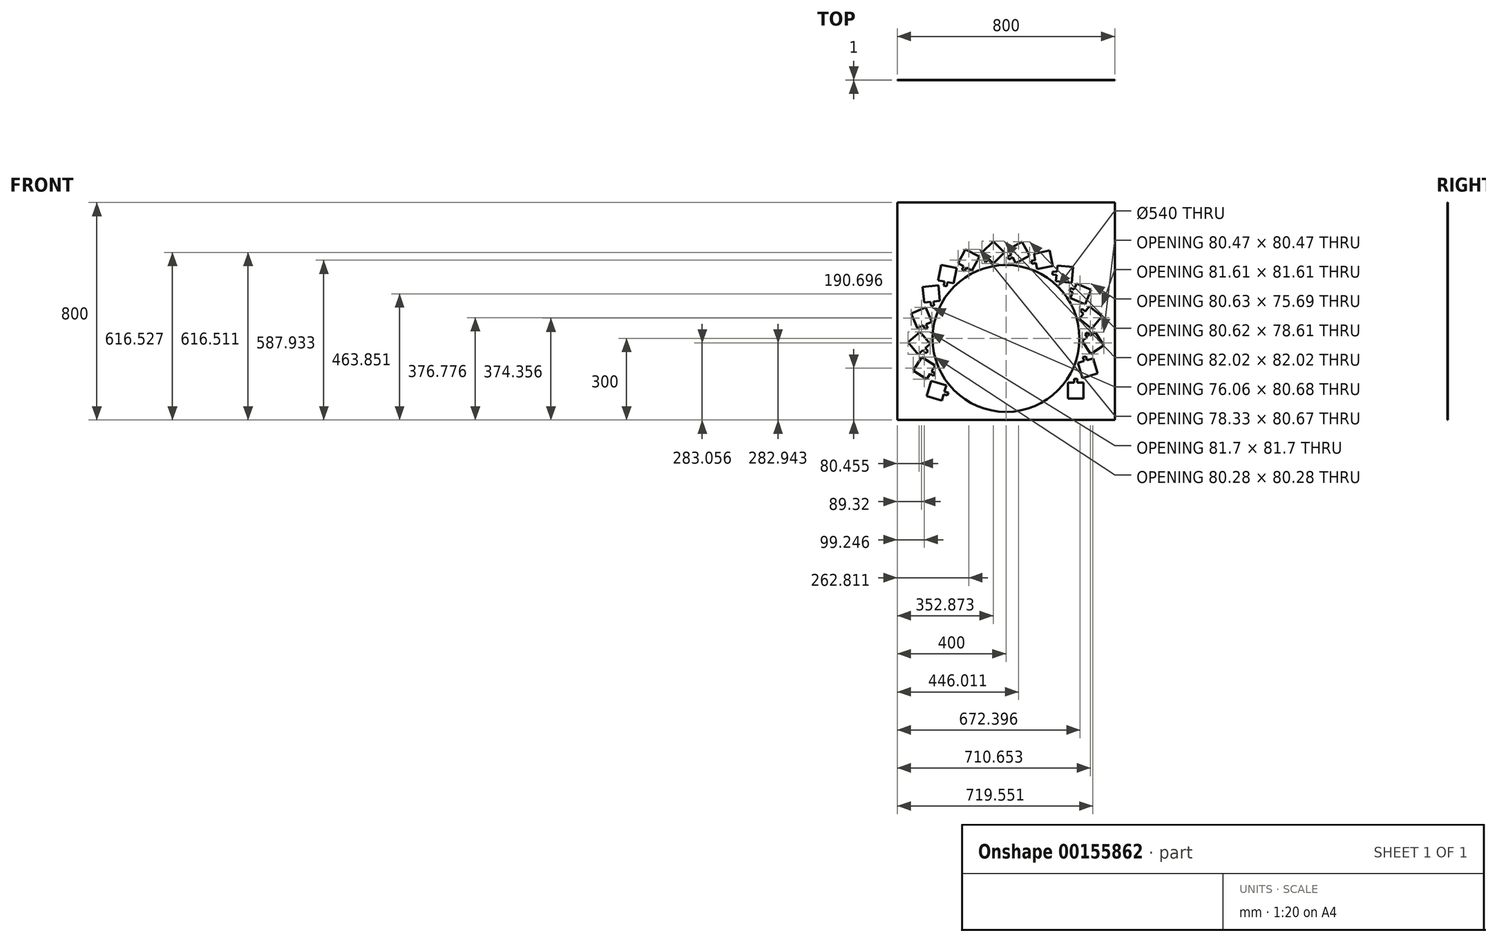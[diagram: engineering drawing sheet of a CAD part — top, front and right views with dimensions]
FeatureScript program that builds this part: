
annotation { "Feature Type Name" : "Feature", "Feature Type Description" : "" }
export const myFeature = defineFeature(function(context is Context, id is Id, definition is map)
    precondition{}
    {
        {
            var Q0;
            Q0=qCreatedBy(makeId("Front.planeOp"),FACE);
            var sketch = newSketch(context, id + "F0", { "sketchPlane" : qUnion([Q0])});
            skLineSegment(sketch, "E0.bottom", {"start": v(-400, 400) * mm, "end": v(400, 400) * mm});
            skLineSegment(sketch, "E0.top", {"start": v(-400, -400) * mm, "end": v(400, -400) * mm});
            skLineSegment(sketch, "E0.left", {"start": v(-400, 400) * mm, "end": v(-400, -400) * mm});
            skLineSegment(sketch, "E0.right", {"start": v(400, 400) * mm, "end": v(400, -400) * mm});
            skPoint(sketch, "E0.middle", {"position": v(0, 0) * mm});
            skSolve(sketch);
        }
        {
            var Q0;
            Q0=makeQuery(id+"F0.imprint","IMPRINT",FACE,{"disambiguationData":[TD([[makeQuery(id+"F0.imprint","IMPRINT",EDGE,{"derivedFrom":sQuery(id+"F0.wireOp",EDGE,"E0.bottom")}),-1.0]])]});
            extrude(context, id + "F1", {"entities" : qUnion([Q0]), "depth" : 1 * mm});
        }
        {
            var Q0;
            Q0=qCreatedBy(makeId("Front.planeOp"),FACE);
            var sketch = newSketch(context, id + "F2", { "sketchPlane" : qUnion([Q0])});
            skCircle(sketch, "E1", {"center": v(0, -100) * mm, "radius": 270 * mm});
            skSolve(sketch);
        }
        {
            var Q0;
            Q0 = qSketchRegion(id + "F2", true);
            extrude(context, id + "F3", {"entities" : qUnion([Q0]), "operationType" : NewBodyOperationType.REMOVE, "depth" : 3 * mm});
        }
        {
            var Q0;
            Q0=makeQuery(id+"F1.opExtrude","CAP_FACE",FACE,{"disambiguationData":[OSD([sQuery(id+"F0.wireOp",EDGE,"E0.bottom"),sQuery(id+"F0.wireOp",EDGE,"E0.top"),sQuery(id+"F0.wireOp",EDGE,"E0.left"),sQuery(id+"F0.wireOp",EDGE,"E0.right")])],"isStart":false});
            var sketch = newSketch(context, id + "F4", { "sketchPlane" : qUnion([Q0])});
            skLineSegment(sketch, "E2", {"start": v(0, -100) * mm, "end": v(400, -400) * mm, "construction": true});
            skLineSegment(sketch, "E3.MirrorCS", {"start": v(0, -100) * mm, "end": v(-400, -400) * mm, "construction": true});
            skCircle(sketch, "E4", {"center": v(0, -100) * mm, "radius": 320 * mm, "construction": true});
            skLineSegment(sketch, "E5.bottom", {"start": v(227, -263) * mm, "end": v(250.5, -263) * mm});
            skLineSegment(sketch, "E5.top", {"start": v(227, -321) * mm, "end": v(285, -321) * mm});
            skLineSegment(sketch, "E5.left", {"start": v(227, -263) * mm, "end": v(227, -321) * mm});
            skLineSegment(sketch, "E5.right", {"start": v(285, -263) * mm, "end": v(285, -321) * mm});
            skPoint(sketch, "E5.middle", {"position": v(256, -292) * mm});
            skLineSegment(sketch, "E6.top", {"start": v(250.5, -248) * mm, "end": v(261.5, -248) * mm});
            skLineSegment(sketch, "E6.left", {"start": v(250.5, -263) * mm, "end": v(250.5, -248) * mm});
            skLineSegment(sketch, "E6.right", {"start": v(261.5, -263) * mm, "end": v(261.5, -248) * mm});
            skLineSegment(sketch, "E7.trimOffspring", {"start": v(261.5, -263) * mm, "end": v(285, -263) * mm});
            skPoint(sketch, "E8.1.0", {"position": v(300.8, -209.2) * mm});
            skLineSegment(sketch, "E8.1.1", {"start": v(297.62, -179.85) * mm, "end": v(320.1, -173.01) * mm});
            skLineSegment(sketch, "E8.1.2", {"start": v(297.62, -179.85) * mm, "end": v(293.25, -165.5) * mm});
            skLineSegment(sketch, "E8.1.3", {"start": v(264.6, -189.9) * mm, "end": v(287.1, -183.05) * mm});
            skLineSegment(sketch, "E8.1.4", {"start": v(320.1, -173.01) * mm, "end": v(336.98, -228.5) * mm});
            skLineSegment(sketch, "E8.1.5", {"start": v(287.1, -183.05) * mm, "end": v(282.73, -168.7) * mm});
            skLineSegment(sketch, "E8.1.6", {"start": v(282.73, -168.7) * mm, "end": v(293.25, -165.5) * mm});
            skLineSegment(sketch, "E8.1.7", {"start": v(281.49, -245.38) * mm, "end": v(336.98, -228.5) * mm});
            skLineSegment(sketch, "E8.1.8", {"start": v(264.6, -189.9) * mm, "end": v(281.49, -245.38) * mm});
            skPoint(sketch, "E8.2.0", {"position": v(319.55, -116.94) * mm});
            skLineSegment(sketch, "E8.2.1", {"start": v(307.97, -89.8) * mm, "end": v(327.5, -76.7) * mm});
            skLineSegment(sketch, "E8.2.2", {"start": v(307.97, -89.8) * mm, "end": v(299.62, -77.33) * mm});
            skLineSegment(sketch, "E8.2.3", {"start": v(279.32, -109) * mm, "end": v(298.84, -95.92) * mm});
            skLineSegment(sketch, "E8.2.4", {"start": v(327.5, -76.7) * mm, "end": v(359.79, -124.89) * mm});
            skLineSegment(sketch, "E8.2.5", {"start": v(298.84, -95.92) * mm, "end": v(290.48, -83.46) * mm});
            skLineSegment(sketch, "E8.2.6", {"start": v(290.48, -83.46) * mm, "end": v(299.62, -77.33) * mm});
            skLineSegment(sketch, "E8.2.7", {"start": v(311.6, -157.18) * mm, "end": v(359.79, -124.89) * mm});
            skLineSegment(sketch, "E8.2.8", {"start": v(279.32, -109) * mm, "end": v(311.6, -157.18) * mm});
            skPoint(sketch, "E8.3.0", {"position": v(310.65, -23.22) * mm});
            skLineSegment(sketch, "E8.3.1", {"start": v(291.67, -0.62) * mm, "end": v(306.54, 17.58) * mm});
            skLineSegment(sketch, "E8.3.2", {"start": v(291.67, -0.62) * mm, "end": v(280.06, 8.87) * mm});
            skLineSegment(sketch, "E8.3.3", {"start": v(269.85, -27.33) * mm, "end": v(284.72, -9.14) * mm});
            skLineSegment(sketch, "E8.3.4", {"start": v(306.54, 17.58) * mm, "end": v(351.46, -19.11) * mm});
            skLineSegment(sketch, "E8.3.5", {"start": v(284.72, -9.14) * mm, "end": v(273.1, 0.35) * mm});
            skLineSegment(sketch, "E8.3.6", {"start": v(273.1, 0.35) * mm, "end": v(280.06, 8.87) * mm});
            skLineSegment(sketch, "E8.3.7", {"start": v(314.76, -64.03) * mm, "end": v(351.46, -19.11) * mm});
            skLineSegment(sketch, "E8.3.8", {"start": v(269.85, -27.33) * mm, "end": v(314.76, -64.03) * mm});
            skPoint(sketch, "E8.4.0", {"position": v(274.87, 63.85) * mm});
            skLineSegment(sketch, "E8.4.1", {"start": v(250.13, 79.96) * mm, "end": v(259.06, 101.7) * mm});
            skLineSegment(sketch, "E8.4.2", {"start": v(250.13, 79.96) * mm, "end": v(236.26, 85.66) * mm});
            skLineSegment(sketch, "E8.4.3", {"start": v(237.03, 48.04) * mm, "end": v(245.95, 69.78) * mm});
            skLineSegment(sketch, "E8.4.4", {"start": v(259.06, 101.7) * mm, "end": v(312.71, 79.66) * mm});
            skLineSegment(sketch, "E8.4.5", {"start": v(245.95, 69.78) * mm, "end": v(232.08, 75.48) * mm});
            skLineSegment(sketch, "E8.4.6", {"start": v(232.08, 75.48) * mm, "end": v(236.26, 85.66) * mm});
            skLineSegment(sketch, "E8.4.7", {"start": v(290.68, 26) * mm, "end": v(312.71, 79.66) * mm});
            skLineSegment(sketch, "E8.4.8", {"start": v(237.03, 48.04) * mm, "end": v(290.68, 26) * mm});
            skPoint(sketch, "E8.5.0", {"position": v(215.3, 136.74) * mm});
            skLineSegment(sketch, "E8.5.1", {"start": v(186.94, 144.96) * mm, "end": v(189.16, 168.35) * mm});
            skLineSegment(sketch, "E8.5.2", {"start": v(186.94, 144.96) * mm, "end": v(172, 146.37) * mm});
            skLineSegment(sketch, "E8.5.3", {"start": v(183.69, 110.61) * mm, "end": v(185.9, 134) * mm});
            skLineSegment(sketch, "E8.5.4", {"start": v(189.16, 168.35) * mm, "end": v(246.9, 162.88) * mm});
            skLineSegment(sketch, "E8.5.5", {"start": v(185.9, 134) * mm, "end": v(170.97, 135.42) * mm});
            skLineSegment(sketch, "E8.5.6", {"start": v(170.97, 135.42) * mm, "end": v(172, 146.37) * mm});
            skLineSegment(sketch, "E8.5.7", {"start": v(241.43, 105.14) * mm, "end": v(246.9, 162.88) * mm});
            skLineSegment(sketch, "E8.5.8", {"start": v(183.69, 110.61) * mm, "end": v(241.43, 105.14) * mm});
            skPoint(sketch, "E8.6.0", {"position": v(137.09, 189.15) * mm});
            skLineSegment(sketch, "E8.6.1", {"start": v(107.57, 188.75) * mm, "end": v(102.89, 211.78) * mm});
            skLineSegment(sketch, "E8.6.2", {"start": v(107.57, 188.75) * mm, "end": v(92.87, 185.76) * mm});
            skLineSegment(sketch, "E8.6.3", {"start": v(114.45, 154.95) * mm, "end": v(109.77, 177.98) * mm});
            skLineSegment(sketch, "E8.6.4", {"start": v(102.89, 211.78) * mm, "end": v(159.72, 223.35) * mm});
            skLineSegment(sketch, "E8.6.5", {"start": v(109.77, 177.98) * mm, "end": v(95.07, 174.98) * mm});
            skLineSegment(sketch, "E8.6.6", {"start": v(95.07, 174.98) * mm, "end": v(92.87, 185.76) * mm});
            skLineSegment(sketch, "E8.6.7", {"start": v(171.29, 166.52) * mm, "end": v(159.72, 223.35) * mm});
            skLineSegment(sketch, "E8.6.8", {"start": v(114.45, 154.95) * mm, "end": v(171.29, 166.52) * mm});
            skPoint(sketch, "E8.7.0", {"position": v(47.01, 216.53) * mm});
            skLineSegment(sketch, "E8.7.1", {"start": v(18.9, 207.56) * mm, "end": v(7.7, 228.23) * mm});
            skLineSegment(sketch, "E8.7.2", {"start": v(18.9, 207.56) * mm, "end": v(5.7, 200.42) * mm});
            skLineSegment(sketch, "E8.7.3", {"start": v(35.31, 177.22) * mm, "end": v(24.13, 197.89) * mm});
            skLineSegment(sketch, "E8.7.4", {"start": v(7.7, 228.23) * mm, "end": v(58.72, 255.83) * mm});
            skLineSegment(sketch, "E8.7.5", {"start": v(24.13, 197.89) * mm, "end": v(10.94, 190.75) * mm});
            skLineSegment(sketch, "E8.7.6", {"start": v(10.94, 190.75) * mm, "end": v(5.7, 200.42) * mm});
            skLineSegment(sketch, "E8.7.7", {"start": v(86.32, 204.83) * mm, "end": v(58.72, 255.83) * mm});
            skLineSegment(sketch, "E8.7.8", {"start": v(35.31, 177.22) * mm, "end": v(86.32, 204.83) * mm});
            skPoint(sketch, "E8.8.0", {"position": v(-47.13, 216.51) * mm});
            skLineSegment(sketch, "E8.8.1", {"start": v(-71.42, 199.75) * mm, "end": v(-88.14, 216.27) * mm});
            skLineSegment(sketch, "E8.8.2", {"start": v(-71.42, 199.75) * mm, "end": v(-81.97, 189.08) * mm});
            skLineSegment(sketch, "E8.8.3", {"start": v(-46.88, 175.5) * mm, "end": v(-63.6, 192.02) * mm});
            skLineSegment(sketch, "E8.8.4", {"start": v(-88.14, 216.27) * mm, "end": v(-47.37, 257.52) * mm});
            skLineSegment(sketch, "E8.8.5", {"start": v(-63.6, 192.02) * mm, "end": v(-74.14, 181.35) * mm});
            skLineSegment(sketch, "E8.8.6", {"start": v(-74.14, 181.35) * mm, "end": v(-81.97, 189.08) * mm});
            skLineSegment(sketch, "E8.8.7", {"start": v(-6.12, 216.75) * mm, "end": v(-47.37, 257.52) * mm});
            skLineSegment(sketch, "E8.8.8", {"start": v(-46.88, 175.5) * mm, "end": v(-6.12, 216.75) * mm});
            skPoint(sketch, "E8.9.0", {"position": v(-137.19, 189.1) * mm});
            skLineSegment(sketch, "E8.9.1", {"start": v(-155.56, 166) * mm, "end": v(-176.36, 176.93) * mm});
            skLineSegment(sketch, "E8.9.2", {"start": v(-155.56, 166) * mm, "end": v(-162.54, 152.72) * mm});
            skLineSegment(sketch, "E8.9.3", {"start": v(-125.02, 149.93) * mm, "end": v(-145.82, 160.87) * mm});
            skLineSegment(sketch, "E8.9.4", {"start": v(-176.36, 176.93) * mm, "end": v(-149.36, 228.27) * mm});
            skLineSegment(sketch, "E8.9.5", {"start": v(-145.82, 160.87) * mm, "end": v(-152.8, 147.6) * mm});
            skLineSegment(sketch, "E8.9.6", {"start": v(-152.8, 147.6) * mm, "end": v(-162.54, 152.72) * mm});
            skLineSegment(sketch, "E8.9.7", {"start": v(-98.02, 201.27) * mm, "end": v(-149.36, 228.27) * mm});
            skLineSegment(sketch, "E8.9.8", {"start": v(-125.02, 149.93) * mm, "end": v(-98.02, 201.27) * mm});
            skPoint(sketch, "E8.10.0", {"position": v(-215.38, 136.67) * mm});
            skLineSegment(sketch, "E8.10.1", {"start": v(-226.23, 109.22) * mm, "end": v(-249.3, 113.63) * mm});
            skLineSegment(sketch, "E8.10.2", {"start": v(-226.23, 109.22) * mm, "end": v(-229.05, 94.49) * mm});
            skLineSegment(sketch, "E8.10.3", {"start": v(-192.34, 102.74) * mm, "end": v(-215.42, 107.15) * mm});
            skLineSegment(sketch, "E8.10.4", {"start": v(-249.3, 113.63) * mm, "end": v(-238.41, 170.6) * mm});
            skLineSegment(sketch, "E8.10.5", {"start": v(-215.42, 107.15) * mm, "end": v(-218.24, 92.42) * mm});
            skLineSegment(sketch, "E8.10.6", {"start": v(-218.24, 92.42) * mm, "end": v(-229.05, 94.49) * mm});
            skLineSegment(sketch, "E8.10.7", {"start": v(-181.45, 159.7) * mm, "end": v(-238.41, 170.6) * mm});
            skLineSegment(sketch, "E8.10.8", {"start": v(-192.34, 102.74) * mm, "end": v(-181.45, 159.7) * mm});
            skPoint(sketch, "E8.11.0", {"position": v(-274.93, 63.75) * mm});
            skLineSegment(sketch, "E8.11.1", {"start": v(-277.32, 34.33) * mm, "end": v(-300.69, 31.84) * mm});
            skLineSegment(sketch, "E8.11.2", {"start": v(-277.32, 34.33) * mm, "end": v(-275.73, 19.42) * mm});
            skLineSegment(sketch, "E8.11.3", {"start": v(-243.01, 38) * mm, "end": v(-266.38, 35.5) * mm});
            skLineSegment(sketch, "E8.11.4", {"start": v(-300.69, 31.84) * mm, "end": v(-306.84, 89.51) * mm});
            skLineSegment(sketch, "E8.11.5", {"start": v(-266.38, 35.5) * mm, "end": v(-264.79, 20.59) * mm});
            skLineSegment(sketch, "E8.11.6", {"start": v(-264.79, 20.59) * mm, "end": v(-275.73, 19.42) * mm});
            skLineSegment(sketch, "E8.11.7", {"start": v(-249.17, 95.67) * mm, "end": v(-306.84, 89.51) * mm});
            skLineSegment(sketch, "E8.11.8", {"start": v(-243.01, 38) * mm, "end": v(-249.17, 95.67) * mm});
            skPoint(sketch, "E8.12.0", {"position": v(-310.68, -23.33) * mm});
            skLineSegment(sketch, "E8.12.1", {"start": v(-304.4, -52.18) * mm, "end": v(-326.04, -61.36) * mm});
            skLineSegment(sketch, "E8.12.2", {"start": v(-304.4, -52.18) * mm, "end": v(-298.54, -65.98) * mm});
            skLineSegment(sketch, "E8.12.3", {"start": v(-272.65, -38.7) * mm, "end": v(-294.28, -47.88) * mm});
            skLineSegment(sketch, "E8.12.4", {"start": v(-326.04, -61.36) * mm, "end": v(-348.7, -7.98) * mm});
            skLineSegment(sketch, "E8.12.5", {"start": v(-294.28, -47.88) * mm, "end": v(-288.42, -61.68) * mm});
            skLineSegment(sketch, "E8.12.6", {"start": v(-288.42, -61.68) * mm, "end": v(-298.54, -65.98) * mm});
            skLineSegment(sketch, "E8.12.7", {"start": v(-295.32, 14.7) * mm, "end": v(-348.7, -7.98) * mm});
            skLineSegment(sketch, "E8.12.8", {"start": v(-272.65, -38.7) * mm, "end": v(-295.32, 14.7) * mm});
            skPoint(sketch, "E8.13.0", {"position": v(-319.55, -117.06) * mm});
            skLineSegment(sketch, "E8.13.1", {"start": v(-305.15, -142.83) * mm, "end": v(-323.17, -157.9) * mm});
            skLineSegment(sketch, "E8.13.2", {"start": v(-305.15, -142.83) * mm, "end": v(-295.52, -154.33) * mm});
            skLineSegment(sketch, "E8.13.3", {"start": v(-278.7, -120.68) * mm, "end": v(-296.72, -135.77) * mm});
            skLineSegment(sketch, "E8.13.4", {"start": v(-323.17, -157.9) * mm, "end": v(-360.4, -113.43) * mm});
            skLineSegment(sketch, "E8.13.5", {"start": v(-296.72, -135.77) * mm, "end": v(-287.09, -147.27) * mm});
            skLineSegment(sketch, "E8.13.6", {"start": v(-287.09, -147.27) * mm, "end": v(-295.52, -154.33) * mm});
            skLineSegment(sketch, "E8.13.7", {"start": v(-315.92, -76.2) * mm, "end": v(-360.4, -113.43) * mm});
            skLineSegment(sketch, "E8.13.8", {"start": v(-278.7, -120.68) * mm, "end": v(-315.92, -76.2) * mm});
            skPoint(sketch, "E8.14.0", {"position": v(-300.75, -209.3) * mm});
            skLineSegment(sketch, "E8.14.1", {"start": v(-279.48, -229.77) * mm, "end": v(-292.34, -249.44) * mm});
            skLineSegment(sketch, "E8.14.2", {"start": v(-279.48, -229.77) * mm, "end": v(-266.93, -237.97) * mm});
            skLineSegment(sketch, "E8.14.3", {"start": v(-260.61, -200.89) * mm, "end": v(-273.47, -220.56) * mm});
            skLineSegment(sketch, "E8.14.4", {"start": v(-292.34, -249.44) * mm, "end": v(-340.9, -217.72) * mm});
            skLineSegment(sketch, "E8.14.5", {"start": v(-273.47, -220.56) * mm, "end": v(-260.9, -228.76) * mm});
            skLineSegment(sketch, "E8.14.6", {"start": v(-260.9, -228.76) * mm, "end": v(-266.93, -237.97) * mm});
            skLineSegment(sketch, "E8.14.7", {"start": v(-309.17, -169.16) * mm, "end": v(-340.9, -217.72) * mm});
            skLineSegment(sketch, "E8.14.8", {"start": v(-260.61, -200.89) * mm, "end": v(-309.17, -169.16) * mm});
            skPoint(sketch, "E8.15.0", {"position": v(-255.93, -292.1) * mm});
            skLineSegment(sketch, "E8.15.1", {"start": v(-229.63, -305.48) * mm, "end": v(-236.2, -328.04) * mm});
            skLineSegment(sketch, "E8.15.2", {"start": v(-229.63, -305.48) * mm, "end": v(-215.23, -309.68) * mm});
            skLineSegment(sketch, "E8.15.3", {"start": v(-219.98, -272.36) * mm, "end": v(-226.55, -294.92) * mm});
            skLineSegment(sketch, "E8.15.4", {"start": v(-236.2, -328.04) * mm, "end": v(-291.89, -311.82) * mm});
            skLineSegment(sketch, "E8.15.5", {"start": v(-226.55, -294.92) * mm, "end": v(-212.15, -299.11) * mm});
            skLineSegment(sketch, "E8.15.6", {"start": v(-212.15, -299.11) * mm, "end": v(-215.23, -309.68) * mm});
            skLineSegment(sketch, "E8.15.7", {"start": v(-275.66, -256.14) * mm, "end": v(-291.89, -311.82) * mm});
            skLineSegment(sketch, "E8.15.8", {"start": v(-219.98, -272.36) * mm, "end": v(-275.66, -256.14) * mm});
            skLineSegment(sketch, "E8.anchor1", {"start": v(0, -100) * mm, "end": v(227, -321) * mm, "construction": true});
            skLineSegment(sketch, "E8.anchor2", {"start": v(0, -100) * mm, "end": v(-275.66, -256.14) * mm, "construction": true});
            skSolve(sketch);
        }
        {
            var Q0;
            Q0 = qSketchRegion(id + "F4", true);
            extrude(context, id + "F5", {"entities" : qUnion([Q0]), "operationType" : NewBodyOperationType.REMOVE, "endBound" : BoundingType.UP_TO_NEXT, "oppositeDirection" : true, "depth" : 25 * mm});
        }
    });
